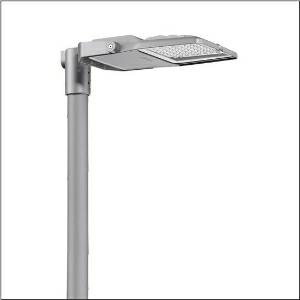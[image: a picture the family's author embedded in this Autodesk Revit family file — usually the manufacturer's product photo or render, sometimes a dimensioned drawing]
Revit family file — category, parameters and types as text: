
# Revit family: floodlight_fl_21_mini___pl43_5xa7775b2a3a_f7a6
name_source: partatom
category: Lighting Fixtures
units: mm (PartAtom-declared; Revit-internal decimal feet)

## family parameters
Cut with Voids When Loaded = No
Host = Face
Light Source = No
Part Type = Normal
Room Calculation Point = No
Round Connector Dimension = Use Diameter
Shared = No

## types (1)
- --- (1 x LED, 6390 lm, 45.7 W, 3000K)
    Apparent Load = 46 VA
    CIE Flux Codes = 27 78 99 100 100
    Color Rendering = 70
    Color Temperature = 3000K
    Default Elevation = 1800 mm
    Description = Floodlight FL 21 mini, floodlight, primary light control with lens, of PMMA, primary optical cover: protective disc, of toughened safety glass, transparent, light distribution: PL43, light emission: direct distribution, installation type: surface-mounted, LED, High Power LED, rated luminous flux: 6.390lm, luminous efficacy: 140lm/W, light colour: 730, colour temperature: 3000K, control gear: Smart Interface (Zhaga), control: flexible luminous flux parameterisation, time-dependent luminous flux control, constant luminous flux control, overheat protection, pre-setting: logarithmic dimming characteristic, with terminal, 6-pole, mains connection: 220..240V, AC, 50/60Hz, start of lifetime: 46W, end of service life: 48W, reduction: 22W, luminaire housing, of diecast aluminium, powder-coated, Siteco® metallic grey (DB 702S), corrosivity category C5 mid according to DIN EN ISO 12944, suitable for swimming pools, chlorine-resistant, sealing non-destructively replaceable, please order mast flange separately, mast bracket, of steel, galvanised, powder-coated, Siteco® metallic grey (DB 702S), Smart Interface above, protection rating (complete): IP66, insulation class (complete): insulation class II (safety insulation), certification: CE, ENEC, VDE, protection symbol: D, impact resistance: IK08, permissible operating ambient temperature: -40..+40°C, permissible operating ambient temperature for outdoor applications: -40..+50°C, standard: DIN EN 12944, LABS conformity tested according to VDMA 24364:2018-05, packaging unit: 1 piece

Light Distribution: PL43
    Height = 70 mm
    Lamp = 1 x LED
    Lamp Light Flux = 6390 lm
    Lamp Power = 45.7 W
    Lamp count = 1
    Length = 485 mm
    Luminous efficacy = 140 lm/W
    Manufacturer = Siteco
    ModVariant = No
    Model = 5XA7775B2A3A
    Number of Poles = 1
    OnlyDefault = Yes
    Power Factor = 1
    Product Name = Floodlight FL 21 mini | PL43
    Product group = floodlight | pylon annexe
    ProductGroupID = 6200
    Protection Class = Protection class II
    Protection Degree = IP 66
    RLX_Detail_Level = 1
    RLX_Emergency_Light_Flux = 0 lm
    RLX_Emergency_Type = 0
    RLX_Emergency_Type_DB = No
    RlxData = <blob elided: 100985 chars, md5=88b2a120>
    Socket = socket
    Standby Power = 0 W
    System Light Flux = 6390 lm
    System Power = 46 W
    Type Comments = factory setting: luminous flux: 100 % | dim-lin: 254 | 463 mA
    Type Image = l_1007125.jpg
    URL = http://relux.com
    VarID = @adj_161258
    Voltage = 0 V
    Weight = 0.00 kg
    Width = 337 mm

## geometry (parser evidence)
native form markers: Blend x4, Sweep x10
no freeform markers — native parametric forms only
